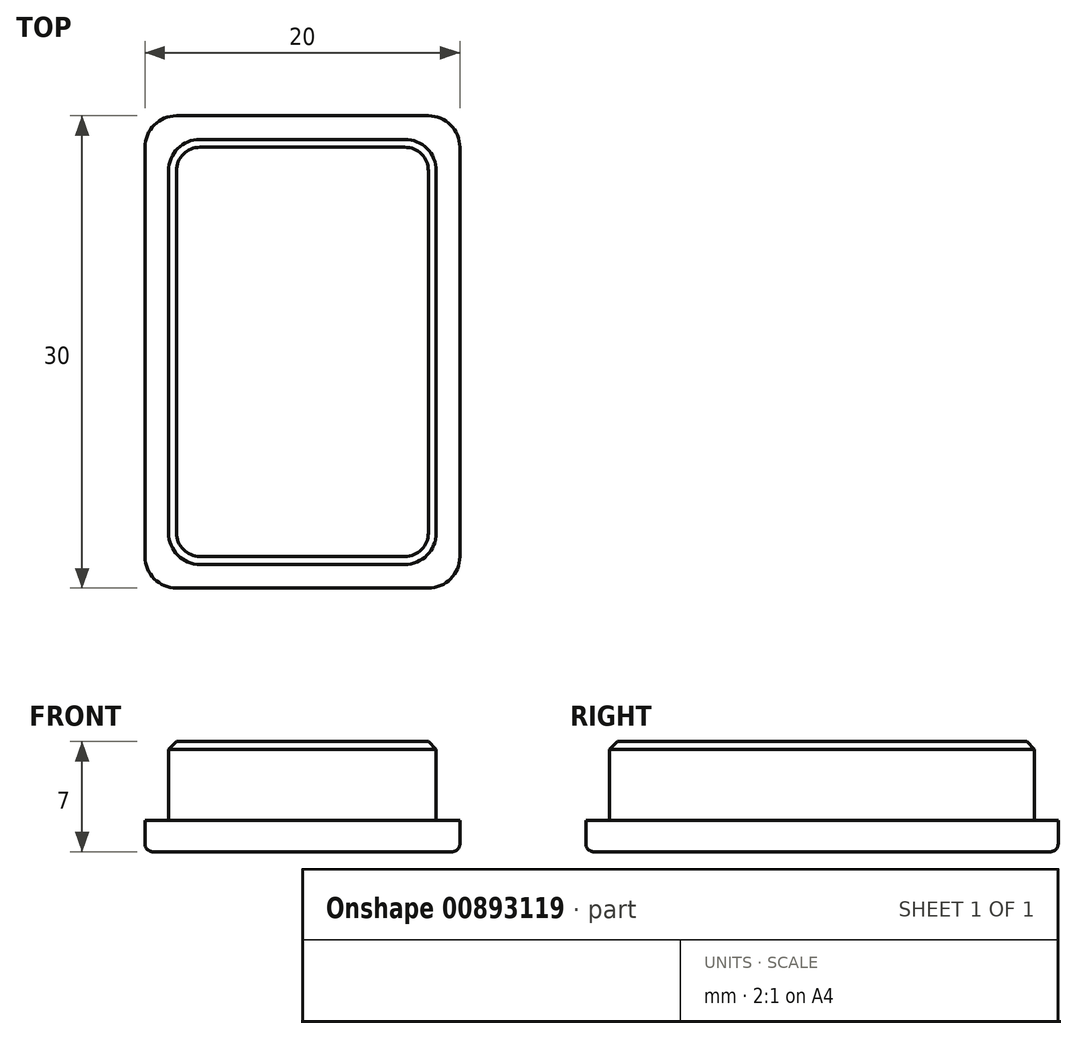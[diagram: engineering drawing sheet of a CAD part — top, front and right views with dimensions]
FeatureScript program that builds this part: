
annotation { "Feature Type Name" : "Feature", "Feature Type Description" : "" }
export const myFeature = defineFeature(function(context is Context, id is Id, definition is map)
    precondition{}
    {
        {
            var Q0;
            Q0=qCreatedBy(makeId("Top.planeOp"),FACE);
            var sketch = newSketch(context, id + "F0", { "sketchPlane" : qUnion([Q0])});
            skLineSegment(sketch, "E0.bottom", {"start": v(-10, 15) * mm, "end": v(10, 15) * mm});
            skLineSegment(sketch, "E0.top", {"start": v(-10, -15) * mm, "end": v(10, -15) * mm});
            skLineSegment(sketch, "E0.left", {"start": v(-10, 15) * mm, "end": v(-10, -15) * mm});
            skLineSegment(sketch, "E0.right", {"start": v(10, 15) * mm, "end": v(10, -15) * mm});
            skPoint(sketch, "E0.middle", {"position": v(0, 0) * mm});
            skSolve(sketch);
        }
        {
            var Q0;
            Q0 = qSketchRegion(id + "F0", true);
            extrude(context, id + "F1", {"entities" : qUnion([Q0]), "depth" : 2 * mm, "offsetDistance" : 25 * mm});
        }
        {
            var Q0;
            Q0=makeQuery(id+"F1.opExtrude","SWEPT_EDGE",EDGE,{"disambiguationData":[OSD([sQuery(id+"F0.wireOp",EDGE,"E0.top"),sQuery(id+"F0.wireOp",EDGE,"E0.left")])]});
            var Q1;
            Q1=makeQuery(id+"F1.opExtrude","SWEPT_EDGE",EDGE,{"disambiguationData":[OSD([sQuery(id+"F0.wireOp",EDGE,"E0.top"),sQuery(id+"F0.wireOp",EDGE,"E0.right")])]});
            var Q2;
            Q2=makeQuery(id+"F1.opExtrude","SWEPT_EDGE",EDGE,{"disambiguationData":[OSD([sQuery(id+"F0.wireOp",EDGE,"E0.bottom"),sQuery(id+"F0.wireOp",EDGE,"E0.left")])]});
            var Q3;
            Q3=makeQuery(id+"F1.opExtrude","SWEPT_EDGE",EDGE,{"disambiguationData":[OSD([sQuery(id+"F0.wireOp",EDGE,"E0.bottom"),sQuery(id+"F0.wireOp",EDGE,"E0.right")])]});
            fillet(context, id + "F2", {"entities" : qUnion([Q0, Q1, Q2, Q3]), "radius" : 2 * mm, "tangentPropagation" : true, "allowEdgeOverflow" : false});
        }
        {
            var Q0;
            Q0=makeQuery(id+"F1.opExtrude","CAP_FACE",FACE,{"disambiguationData":[OSD([sQuery(id+"F0.wireOp",EDGE,"E0.bottom"),sQuery(id+"F0.wireOp",EDGE,"E0.top"),sQuery(id+"F0.wireOp",EDGE,"E0.left"),sQuery(id+"F0.wireOp",EDGE,"E0.right")])],"isStart":false});
            var sketch = newSketch(context, id + "F3", { "sketchPlane" : qUnion([Q0])});
            skLineSegment(sketch, "E1.bottom", {"start": v(-8.5, 13.5) * mm, "end": v(8.5, 13.5) * mm});
            skLineSegment(sketch, "E1.top", {"start": v(-8.5, -13.5) * mm, "end": v(8.5, -13.5) * mm});
            skLineSegment(sketch, "E1.left", {"start": v(-8.5, 13.5) * mm, "end": v(-8.5, -13.5) * mm});
            skLineSegment(sketch, "E1.right", {"start": v(8.5, 13.5) * mm, "end": v(8.5, -13.5) * mm});
            skPoint(sketch, "E1.middle", {"position": v(0, 0) * mm});
            skSolve(sketch);
        }
        {
            var Q0;
            Q0 = qSketchRegion(id + "F3", true);
            extrude(context, id + "F4", {"entities" : qUnion([Q0]), "operationType" : NewBodyOperationType.ADD, "depth" : 5 * mm, "offsetDistance" : 25 * mm});
        }
        {
            var Q0;
            Q0=makeQuery(id+"F4.opExtrude","SWEPT_EDGE",EDGE,{"disambiguationData":[OSD([sQuery(id+"F3.wireOp",EDGE,"E1.top"),sQuery(id+"F3.wireOp",EDGE,"E1.left")])]});
            var Q1;
            Q1=makeQuery(id+"F4.opExtrude","SWEPT_EDGE",EDGE,{"disambiguationData":[OSD([sQuery(id+"F3.wireOp",EDGE,"E1.top"),sQuery(id+"F3.wireOp",EDGE,"E1.right")])]});
            var Q2;
            Q2=makeQuery(id+"F4.opExtrude","SWEPT_EDGE",EDGE,{"disambiguationData":[OSD([sQuery(id+"F3.wireOp",EDGE,"E1.bottom"),sQuery(id+"F3.wireOp",EDGE,"E1.left")])]});
            var Q3;
            Q3=makeQuery(id+"F4.opExtrude","SWEPT_EDGE",EDGE,{"disambiguationData":[OSD([sQuery(id+"F3.wireOp",EDGE,"E1.bottom"),sQuery(id+"F3.wireOp",EDGE,"E1.right")])]});
            fillet(context, id + "F5", {"entities" : qUnion([Q0, Q1, Q2, Q3]), "radius" : 2 * mm, "tangentPropagation" : true, "allowEdgeOverflow" : false});
        }
        {
            var Q0;
            Q0=makeQuery(id+"F4.opExtrude","CAP_EDGE",EDGE,{"disambiguationData":[OSD([sQuery(id+"F3.wireOp",EDGE,"E1.left")])],"isStart":false});
            chamfer(context, id + "F6", {"entities" : qUnion([Q0]), "width" : 0.5 * mm, "tangentPropagation" : true});
        }
        {
            var Q0;
            Q0=makeQuery(id+"F1.opExtrude","CAP_FACE",FACE,{"disambiguationData":[OSD([sQuery(id+"F0.wireOp",EDGE,"E0.bottom"),sQuery(id+"F0.wireOp",EDGE,"E0.top"),sQuery(id+"F0.wireOp",EDGE,"E0.left"),sQuery(id+"F0.wireOp",EDGE,"E0.right")])],"isStart":true});
            fillet(context, id + "F7", {"entities" : qUnion([Q0]), "radius" : 0.5 * mm, "tangentPropagation" : true, "allowEdgeOverflow" : false});
        }
    });
